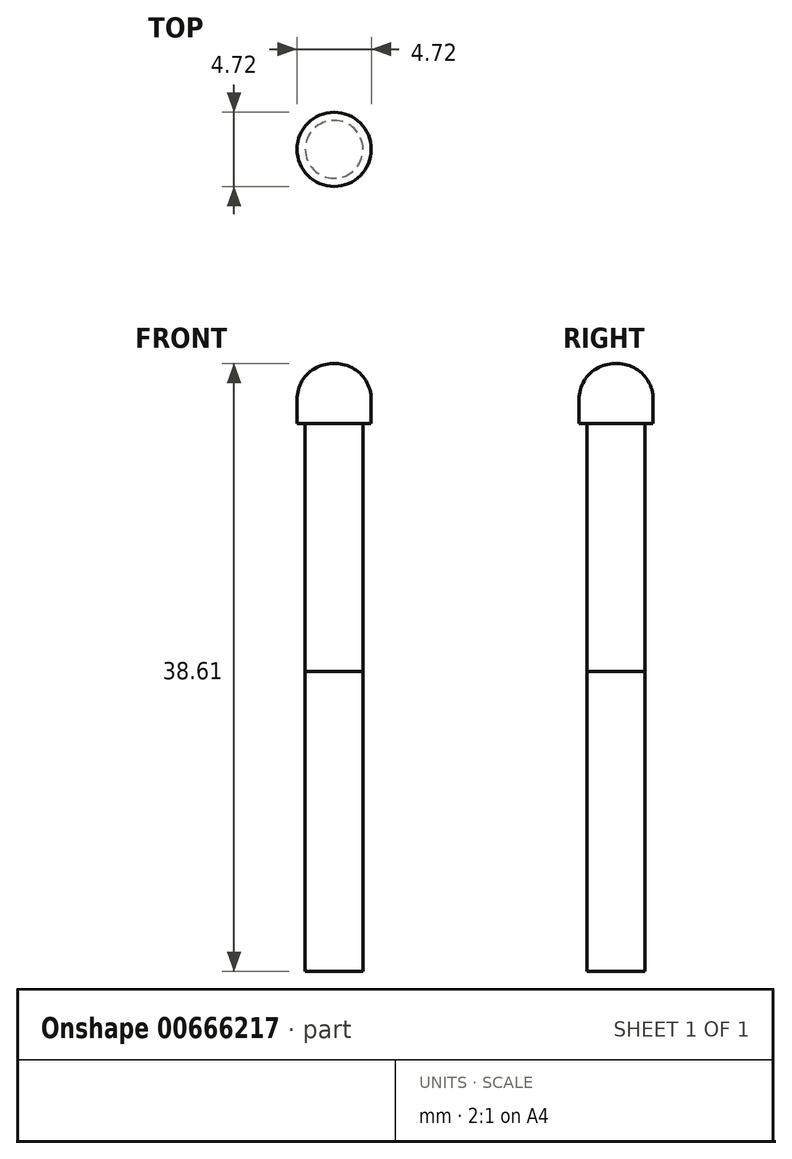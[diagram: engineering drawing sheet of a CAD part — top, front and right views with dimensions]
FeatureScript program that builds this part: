
annotation { "Feature Type Name" : "Feature", "Feature Type Description" : "" }
export const myFeature = defineFeature(function(context is Context, id is Id, definition is map)
    precondition{}
    {
        {
            var Q0;
            Q0=qCreatedBy(makeId("Top.planeOp"),FACE);
            var sketch = newSketch(context, id + "F0", { "sketchPlane" : qUnion([Q0])});
            skCircle(sketch, "E0", {"center": v(0, 0) * mm, "radius": 1.84 * mm});
            skSolve(sketch);
        }
        {
            var Q0;
            Q0=makeQuery(id+"F0.imprint","IMPRINT",FACE,{"disambiguationData":[TD([[makeQuery(id+"F0.imprint","IMPRINT",EDGE,{"derivedFrom":sQuery(id+"F0.wireOp",EDGE,"E0")}),1.0]])]});
            extrude(context, id + "F1", {"entities" : qUnion([Q0]), "depth" : 15.75 * mm, "offsetDistance" : 25.4 * mm});
        }
        {
            var Q0;
            Q0=makeQuery(id+"F1.opExtrude","CAP_FACE",FACE,{"disambiguationData":[OSD([sQuery(id+"F0.wireOp",EDGE,"E0")])],"isStart":false});
            var sketch = newSketch(context, id + "F2", { "sketchPlane" : qUnion([Q0])});
            skCircle(sketch, "E1", {"center": v(0, 0) * mm, "radius": 2.36 * mm});
            skSolve(sketch);
        }
        {
            var Q0;
            Q0=makeQuery(id+"F2.imprint","IMPRINT",FACE,{"disambiguationData":[TD([[makeQuery(id+"F2.imprint","IMPRINT",EDGE,{"derivedFrom":sQuery(id+"F2.wireOp",EDGE,"E1")}),1.0]])]});
            var Q1;
            Q1=makeQuery(id+"F2.imprint","IMPRINT",FACE,{"disambiguationData":[TD([[makeQuery(id+"F2.imprint","IMPRINT",EDGE,{"derivedFrom":makeQuery(id+"F1.opExtrude","CAP_EDGE",EDGE,{"disambiguationData":[OSD([sQuery(id+"F0.wireOp",EDGE,"E0")])],"isStart":false})}),1.0]])]});
            extrude(context, id + "F3", {"entities" : qUnion([Q0, Q1]), "depth" : 3.8 * mm, "offsetDistance" : 25.4 * mm});
        }
        {
            var Q0;
            Q0=makeQuery(id+"F3.opExtrude","CAP_FACE",FACE,{"disambiguationData":[OSD([sQuery(id+"F2.wireOp",EDGE,"E1")])],"isStart":false});
            fillet(context, id + "F4", {"entities" : qUnion([Q0]), "radius" : 2.27 * mm, "tangentPropagation" : true, "allowEdgeOverflow" : false});
        }
        {
            var Q0;
            Q0=makeQuery(id+"F1.opExtrude","CAP_FACE",FACE,{"disambiguationData":[OSD([sQuery(id+"F0.wireOp",EDGE,"E0")])],"isStart":true});
            var sketch = newSketch(context, id + "F5", { "sketchPlane" : qUnion([Q0])});
            skCircle(sketch, "E2", {"center": v(0, 0) * mm, "radius": 1.88 * mm});
            skSolve(sketch);
        }
        {
            var Q0;
            Q0=makeQuery(id+"F5.imprint","IMPRINT",FACE,{"disambiguationData":[TD([[makeQuery(id+"F5.imprint","IMPRINT",EDGE,{"derivedFrom":makeQuery(id+"F1.opExtrude","CAP_EDGE",EDGE,{"disambiguationData":[OSD([sQuery(id+"F0.wireOp",EDGE,"E0")])],"isStart":true})}),-1.0]])]});
            extrude(context, id + "F6", {"entities" : qUnion([Q0]), "depth" : 19.05 * mm, "offsetDistance" : 25.4 * mm});
        }
    });
